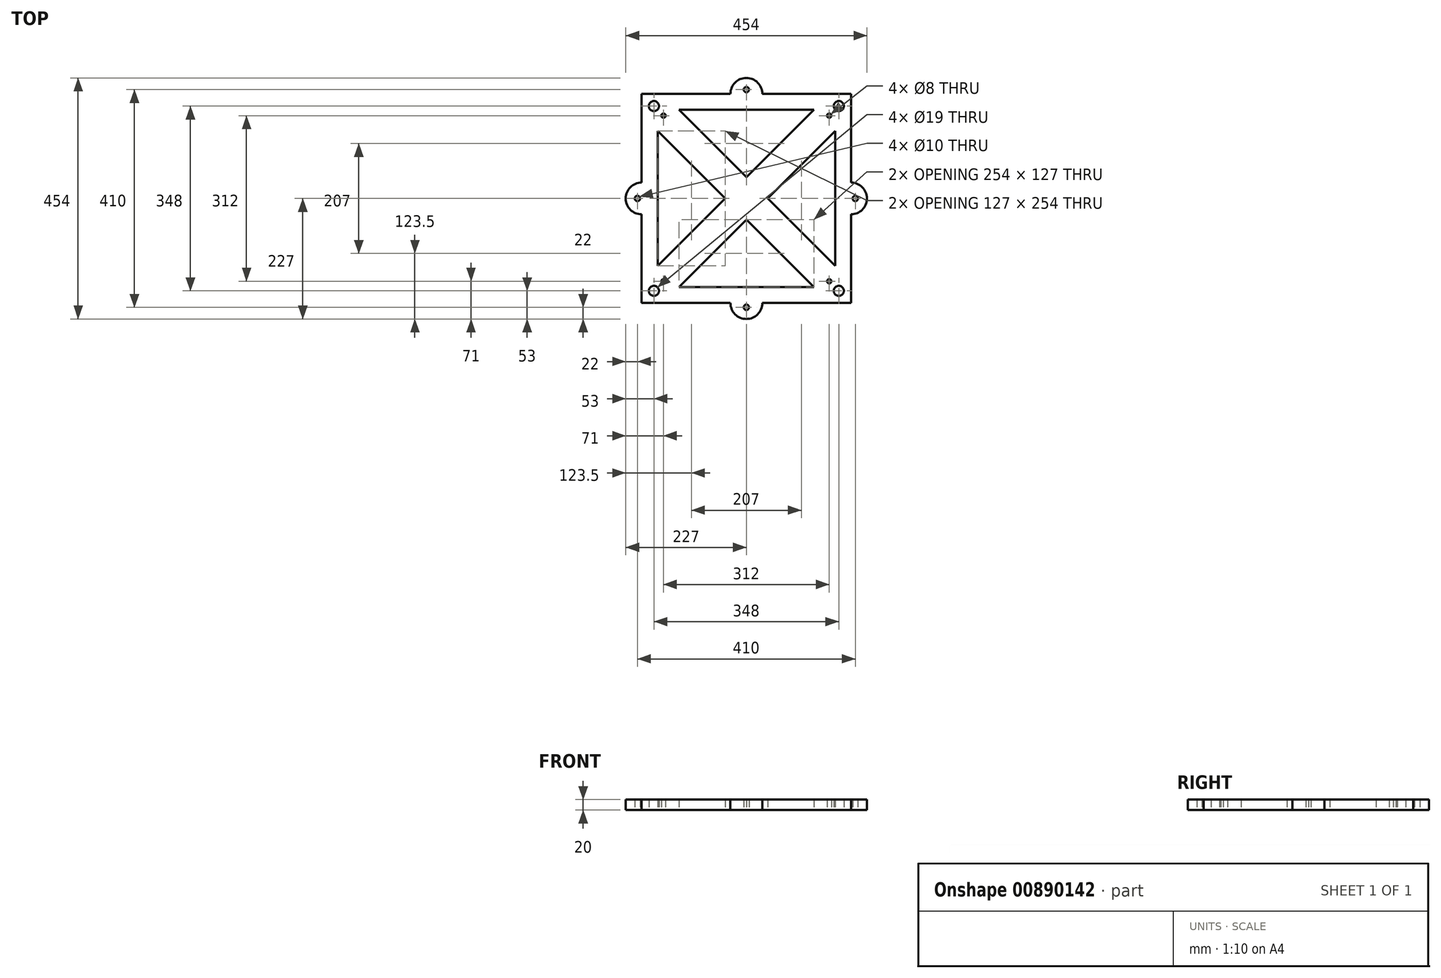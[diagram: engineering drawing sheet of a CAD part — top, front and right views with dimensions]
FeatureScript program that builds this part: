
annotation { "Feature Type Name" : "Feature", "Feature Type Description" : "" }
export const myFeature = defineFeature(function(context is Context, id is Id, definition is map)
    precondition{}
    {
        {
            var Q0;
            Q0=qCreatedBy(makeId("Top.planeOp"),FACE);
            var sketch = newSketch(context, id + "F0", { "sketchPlane" : qUnion([Q0])});
            skLineSegment(sketch, "E0", {"start": v(-167, 127) * mm, "end": v(-127, 167) * mm});
            skLineSegment(sketch, "E1", {"start": v(-127, 167) * mm, "end": v(-127, 197) * mm});
            skLineSegment(sketch, "E2", {"start": v(-127, 197) * mm, "end": v(-197, 197) * mm});
            skLineSegment(sketch, "E3", {"start": v(-197, 197) * mm, "end": v(-197, 127) * mm});
            skLineSegment(sketch, "E4", {"start": v(-197, 127) * mm, "end": v(-167, 127) * mm});
            skCircle(sketch, "E5", {"center": v(-174, 174) * mm, "radius": 9.5 * mm});
            skCircle(sketch, "E6", {"center": v(-156, 156) * mm, "radius": 4 * mm});
            skLineSegment(sketch, "E7.MirrorCS", {"start": v(167, 127) * mm, "end": v(127, 167) * mm});
            skLineSegment(sketch, "E8.MirrorCS", {"start": v(127, 167) * mm, "end": v(127, 197) * mm});
            skLineSegment(sketch, "E9.MirrorCS", {"start": v(127, 197) * mm, "end": v(197, 197) * mm});
            skLineSegment(sketch, "E10.MirrorCS", {"start": v(197, 127) * mm, "end": v(167, 127) * mm});
            skLineSegment(sketch, "E11.MirrorCS", {"start": v(197, 197) * mm, "end": v(197, 127) * mm});
            skCircle(sketch, "E12.MirrorC", {"center": v(174, 174) * mm, "radius": 9.5 * mm});
            skCircle(sketch, "E13.MirrorC", {"center": v(156, 156) * mm, "radius": 4 * mm});
            skLineSegment(sketch, "E14.MirrorCS", {"start": v(127, -167) * mm, "end": v(127, -197) * mm});
            skLineSegment(sketch, "E15.MirrorCS", {"start": v(127, -197) * mm, "end": v(197, -197) * mm});
            skCircle(sketch, "E16.MirrorC", {"center": v(174, -174) * mm, "radius": 9.5 * mm});
            skCircle(sketch, "E17.MirrorC", {"center": v(156, -156) * mm, "radius": 4 * mm});
            skLineSegment(sketch, "E18.MirrorCS", {"start": v(167, -127) * mm, "end": v(127, -167) * mm});
            skLineSegment(sketch, "E19.MirrorCS", {"start": v(-127, -197) * mm, "end": v(-197, -197) * mm});
            skLineSegment(sketch, "E20.MirrorCS", {"start": v(-197, -127) * mm, "end": v(-167, -127) * mm});
            skCircle(sketch, "E21.MirrorC", {"center": v(-174, -174) * mm, "radius": 9.5 * mm});
            skCircle(sketch, "E22.MirrorC", {"center": v(-156, -156) * mm, "radius": 4 * mm});
            skLineSegment(sketch, "E23.MirrorCS", {"start": v(-197, -197) * mm, "end": v(-197, -127) * mm});
            skLineSegment(sketch, "E24.MirrorCS", {"start": v(-127, -167) * mm, "end": v(-127, -197) * mm});
            skLineSegment(sketch, "E25.MirrorCS", {"start": v(197, -127) * mm, "end": v(167, -127) * mm});
            skLineSegment(sketch, "E26.MirrorCS", {"start": v(197, -197) * mm, "end": v(197, -127) * mm});
            skLineSegment(sketch, "E27.MirrorCS", {"start": v(-167, -127) * mm, "end": v(-127, -167) * mm});
            skLineSegment(sketch, "E28", {"start": v(-197, 127) * mm, "end": v(-197, -127) * mm});
            skLineSegment(sketch, "E29", {"start": v(-167, 127) * mm, "end": v(-167, -127) * mm});
            skLineSegment(sketch, "E30", {"start": v(-127, 167) * mm, "end": v(127, 167) * mm});
            skLineSegment(sketch, "E31", {"start": v(-127, 197) * mm, "end": v(127, 197) * mm});
            skLineSegment(sketch, "E32", {"start": v(167, 127) * mm, "end": v(167, -127) * mm});
            skLineSegment(sketch, "E33", {"start": v(197, 127) * mm, "end": v(197, -127) * mm});
            skLineSegment(sketch, "E34", {"start": v(127, -167) * mm, "end": v(-127, -167) * mm});
            skLineSegment(sketch, "E35", {"start": v(-127, -197) * mm, "end": v(127, -197) * mm});
            skLineSegment(sketch, "E36", {"start": v(-167, 127) * mm, "end": v(127, -167) * mm});
            skLineSegment(sketch, "E37", {"start": v(-127, 167) * mm, "end": v(167, -127) * mm});
            skLineSegment(sketch, "E38", {"start": v(127, 167) * mm, "end": v(-167, -127) * mm});
            skLineSegment(sketch, "E39", {"start": v(167, 127) * mm, "end": v(-127, -167) * mm});
            skArc(sketch, "E40", {"start": v(-197, 30) * mm, "mid": v(-227, 0) * mm, "end": v(-197, -30) * mm});
            skArc(sketch, "E41.MirrorCS", {"start": v(197, 30) * mm, "mid": v(227, 0) * mm, "end": v(197, -30) * mm});
            skCircle(sketch, "E42", {"center": v(-205, 0) * mm, "radius": 5 * mm});
            skCircle(sketch, "E43.MirrorC", {"center": v(205, 0) * mm, "radius": 5 * mm});
            skArc(sketch, "E44", {"start": v(30, 197) * mm, "mid": v(0, 227) * mm, "end": v(-30, 197) * mm});
            skCircle(sketch, "E45", {"center": v(0, 205) * mm, "radius": 5 * mm});
            skArc(sketch, "E46.MirrorCS", {"start": v(30, -197) * mm, "mid": v(0, -227) * mm, "end": v(-30, -197) * mm});
            skCircle(sketch, "E47.MirrorC", {"center": v(0, -205) * mm, "radius": 5 * mm});
            skSolve(sketch);
        }
        {
            var Q0;
            Q0=qSketchRegion(id+"F0",true);
            var Q1;
            {var subQ0=sQuery(id+"F0.wireOp",EDGE,"E18.MirrorCS");Q1=makeQuery(id+"F0.imprint","IMPRINT",FACE,{"disambiguationData":[TD([[makeQuery(id+"F0.imprint","IMPRINT",EDGE,{"derivedFrom":subQ0}),-1.0]])]});}
            var Q2;
            {var subQ0=sQuery(id+"F0.wireOp",EDGE,"E27.MirrorCS");Q2=makeQuery(id+"F0.imprint","IMPRINT",FACE,{"disambiguationData":[TD([[makeQuery(id+"F0.imprint","IMPRINT",EDGE,{"derivedFrom":subQ0}),1.0]])]});}
            var Q3;
            {var subQ0=sQuery(id+"F0.wireOp",EDGE,"E0");Q3=makeQuery(id+"F0.imprint","IMPRINT",FACE,{"disambiguationData":[TD([[makeQuery(id+"F0.imprint","IMPRINT",EDGE,{"derivedFrom":subQ0}),-1.0]])]});}
            var Q4;
            {var subQ0=sQuery(id+"F0.wireOp",EDGE,"E38");var subQ1=sQuery(id+"F0.wireOp",EDGE,"E36");var subQ2=makeQuery(id+"F0.imprint","INTERSECT",VERTEX,{"derivedFrom":[subQ1,subQ0]});Q4=makeQuery(id+"F0.imprint","IMPRINT",FACE,{"disambiguationData":[TD([[makeQuery(id+"F0.imprint","IMPRINT",EDGE,{"disambiguationData":[TD([[subQ2,-1.0]])],"derivedFrom":subQ1}),1.0]])]});}
            var Q5;
            {var subQ0=sQuery(id+"F0.wireOp",EDGE,"E7.MirrorCS");Q5=makeQuery(id+"F0.imprint","IMPRINT",FACE,{"disambiguationData":[TD([[makeQuery(id+"F0.imprint","IMPRINT",EDGE,{"derivedFrom":subQ0}),1.0]])]});}
            extrude(context, id + "F1", {"entities" : qUnion([Q0, Q1, Q2, Q3, Q4, Q5]), "depth" : 20 * mm, "offsetDistance" : 25 * mm});
        }
    });
